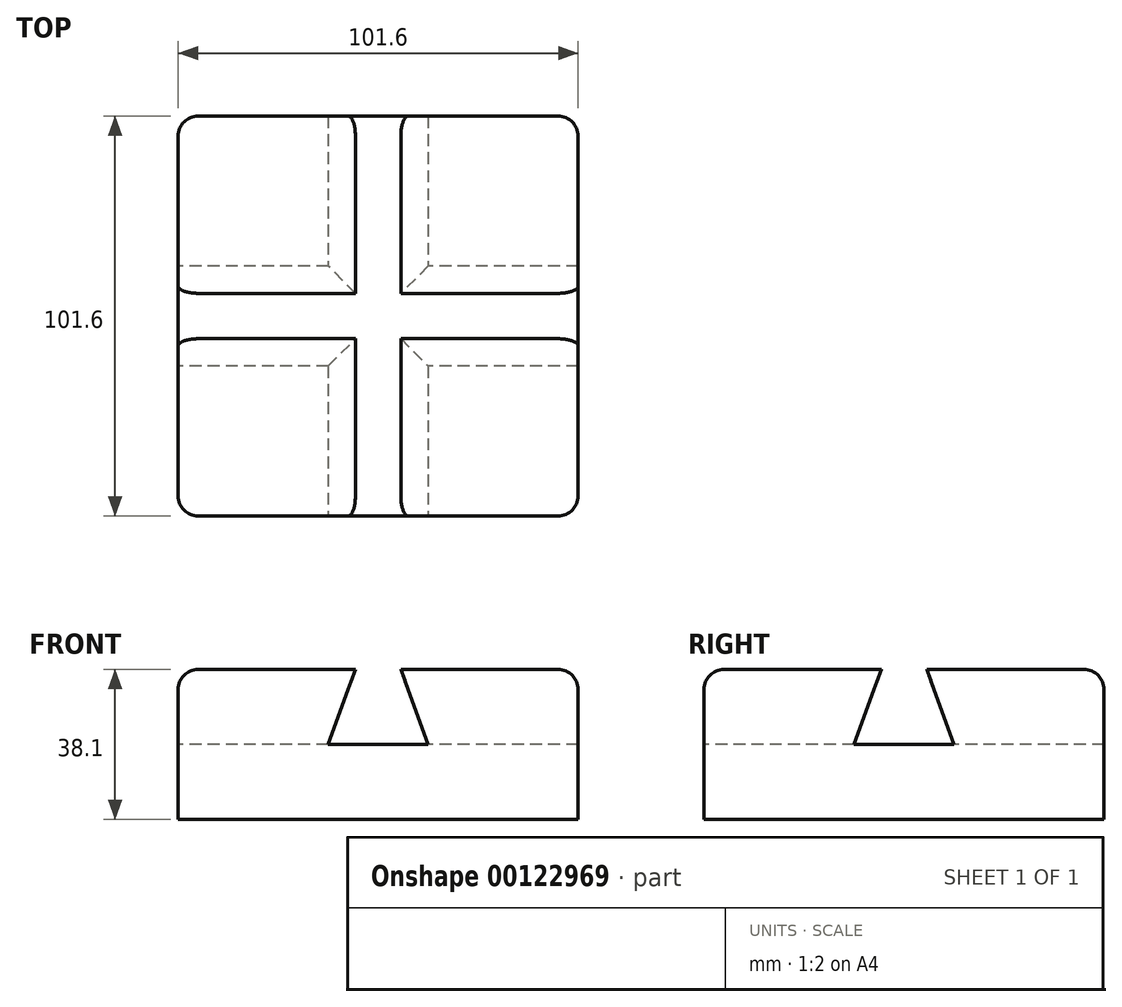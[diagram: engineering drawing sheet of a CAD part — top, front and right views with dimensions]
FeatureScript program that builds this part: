
annotation { "Feature Type Name" : "Feature", "Feature Type Description" : "" }
export const myFeature = defineFeature(function(context is Context, id is Id, definition is map)
    precondition{}
    {
        {
            var Q0;
            Q0=qCreatedBy(makeId("Top.planeOp"),FACE);
            var sketch = newSketch(context, id + "F0", { "sketchPlane" : qUnion([Q0])});
            skLineSegment(sketch, "E0.bottom", {"start": v(-46.22, -52.3) * mm, "end": v(55.38, -52.3) * mm});
            skLineSegment(sketch, "E0.top", {"start": v(-46.22, 49.3) * mm, "end": v(55.38, 49.3) * mm});
            skLineSegment(sketch, "E0.left", {"start": v(-46.22, -52.3) * mm, "end": v(-46.22, 49.3) * mm});
            skLineSegment(sketch, "E0.right", {"start": v(55.38, -52.3) * mm, "end": v(55.38, 49.3) * mm});
            skSolve(sketch);
        }
        {
            var Q0;
            Q0 = qSketchRegion(id + "F0", true);
            extrude(context, id + "F1", {"entities" : qUnion([Q0]), "depth" : 38.1 * mm});
        }
        {
            var Q0;
            Q0=makeQuery(id+"F1.opExtrude","SWEPT_FACE",FACE,{"disambiguationData":[OSD([sQuery(id+"F0.wireOp",EDGE,"E0.bottom")])]});
            var sketch = newSketch(context, id + "F2", { "sketchPlane" : qUnion([Q0])});
            skLineSegment(sketch, "E1", {"start": v(-1.19, 38.1) * mm, "end": v(-8.12, 19.05) * mm});
            skLineSegment(sketch, "E2", {"start": v(-8.12, 19.05) * mm, "end": v(17.28, 19.05) * mm});
            skLineSegment(sketch, "E3", {"start": v(17.28, 19.05) * mm, "end": v(10.34, 38.1) * mm});
            skSolve(sketch);
        }
        {
            var Q0;
            {var subQ0=sQuery(id+"F2.wireOp",EDGE,"E1");Q0=makeQuery(id+"F2.imprint","IMPRINT",FACE,{"disambiguationData":[TD([[makeQuery(id+"F2.imprint","IMPRINT",EDGE,{"derivedFrom":subQ0}),1.0]])]});}
            extrude(context, id + "F3", {"entities" : qUnion([Q0]), "operationType" : NewBodyOperationType.REMOVE, "endBound" : BoundingType.THROUGH_ALL, "oppositeDirection" : true, "depth" : 25.4 * mm});
        }
        {
            var Q0;
            Q0=makeQuery(id+"F1.opExtrude","SWEPT_FACE",FACE,{"disambiguationData":[OSD([sQuery(id+"F0.wireOp",EDGE,"E0.left")])]});
            var sketch = newSketch(context, id + "F4", { "sketchPlane" : qUnion([Q0])});
            skLineSegment(sketch, "E4", {"start": v(-4.26, 38.1) * mm, "end": v(-11.2, 19.05) * mm});
            skLineSegment(sketch, "E5", {"start": v(-11.2, 19.05) * mm, "end": v(14.2, 19.05) * mm});
            skLineSegment(sketch, "E6", {"start": v(14.2, 19.05) * mm, "end": v(7.27, 38.1) * mm});
            skSolve(sketch);
        }
        {
            var Q0;
            {var subQ0=sQuery(id+"F4.wireOp",EDGE,"E4");Q0=makeQuery(id+"F4.imprint","IMPRINT",FACE,{"disambiguationData":[TD([[makeQuery(id+"F4.imprint","IMPRINT",EDGE,{"derivedFrom":subQ0}),1.0]])]});}
            extrude(context, id + "F5", {"entities" : qUnion([Q0]), "operationType" : NewBodyOperationType.REMOVE, "endBound" : BoundingType.THROUGH_ALL, "oppositeDirection" : true, "depth" : 25.4 * mm});
        }
        {
            var Q0;
            {var subQ0=sQuery(id+"F0.wireOp",EDGE,"E0.bottom");var subQ1=sQuery(id+"F0.wireOp",EDGE,"E0.left");Q0=makeQuery(id+"F3.boolean.opBoolean","SPLIT",EDGE,{"disambiguationData":[TD([makeQuery(id+"F1.opExtrude","SWEPT_FACE",FACE,{"disambiguationData":[OSD([subQ1])]})])],"derivedFrom":makeQuery(id+"F1.opExtrude","CAP_EDGE",EDGE,{"disambiguationData":[OSD([subQ0])],"isStart":false})});}
            var Q1;
            {var subQ0=sQuery(id+"F0.wireOp",EDGE,"E0.bottom");var subQ1=sQuery(id+"F0.wireOp",EDGE,"E0.left");Q1=makeQuery(id+"F5.boolean.opBoolean","SPLIT",EDGE,{"disambiguationData":[TD([makeQuery(id+"F1.opExtrude","SWEPT_FACE",FACE,{"disambiguationData":[OSD([subQ0])]})])],"derivedFrom":makeQuery(id+"F1.opExtrude","CAP_EDGE",EDGE,{"disambiguationData":[OSD([subQ1])],"isStart":false})});}
            var Q2;
            {var subQ0=sQuery(id+"F0.wireOp",EDGE,"E0.bottom");var subQ1=sQuery(id+"F0.wireOp",EDGE,"E0.right");Q2=makeQuery(id+"F3.boolean.opBoolean","SPLIT",EDGE,{"disambiguationData":[TD([makeQuery(id+"F1.opExtrude","SWEPT_FACE",FACE,{"disambiguationData":[OSD([subQ1])]})])],"derivedFrom":makeQuery(id+"F1.opExtrude","CAP_EDGE",EDGE,{"disambiguationData":[OSD([subQ0])],"isStart":false})});}
            var Q3;
            {var subQ0=sQuery(id+"F0.wireOp",EDGE,"E0.bottom");var subQ1=sQuery(id+"F0.wireOp",EDGE,"E0.right");Q3=makeQuery(id+"F5.boolean.opBoolean","SPLIT",EDGE,{"disambiguationData":[TD([makeQuery(id+"F1.opExtrude","SWEPT_FACE",FACE,{"disambiguationData":[OSD([subQ0])]})])],"derivedFrom":makeQuery(id+"F1.opExtrude","CAP_EDGE",EDGE,{"disambiguationData":[OSD([subQ1])],"isStart":false})});}
            var Q4;
            {var subQ0=sQuery(id+"F0.wireOp",EDGE,"E0.right");var subQ1=sQuery(id+"F0.wireOp",EDGE,"E0.top");Q4=makeQuery(id+"F5.boolean.opBoolean","SPLIT",EDGE,{"disambiguationData":[TD([makeQuery(id+"F1.opExtrude","SWEPT_FACE",FACE,{"disambiguationData":[OSD([subQ1])]})])],"derivedFrom":makeQuery(id+"F1.opExtrude","CAP_EDGE",EDGE,{"disambiguationData":[OSD([subQ0])],"isStart":false})});}
            var Q5;
            {var subQ0=sQuery(id+"F0.wireOp",EDGE,"E0.right");var subQ1=sQuery(id+"F0.wireOp",EDGE,"E0.top");Q5=makeQuery(id+"F3.boolean.opBoolean","SPLIT",EDGE,{"disambiguationData":[TD([makeQuery(id+"F1.opExtrude","SWEPT_FACE",FACE,{"disambiguationData":[OSD([subQ0])]})])],"derivedFrom":makeQuery(id+"F1.opExtrude","CAP_EDGE",EDGE,{"disambiguationData":[OSD([subQ1])],"isStart":false})});}
            var Q6;
            {var subQ0=sQuery(id+"F0.wireOp",EDGE,"E0.left");var subQ1=sQuery(id+"F0.wireOp",EDGE,"E0.top");Q6=makeQuery(id+"F3.boolean.opBoolean","SPLIT",EDGE,{"disambiguationData":[TD([makeQuery(id+"F1.opExtrude","SWEPT_FACE",FACE,{"disambiguationData":[OSD([subQ0])]})])],"derivedFrom":makeQuery(id+"F1.opExtrude","CAP_EDGE",EDGE,{"disambiguationData":[OSD([subQ1])],"isStart":false})});}
            var Q7;
            {var subQ0=sQuery(id+"F0.wireOp",EDGE,"E0.left");var subQ1=sQuery(id+"F0.wireOp",EDGE,"E0.top");Q7=makeQuery(id+"F5.boolean.opBoolean","SPLIT",EDGE,{"disambiguationData":[TD([makeQuery(id+"F1.opExtrude","SWEPT_FACE",FACE,{"disambiguationData":[OSD([subQ1])]})])],"derivedFrom":makeQuery(id+"F1.opExtrude","CAP_EDGE",EDGE,{"disambiguationData":[OSD([subQ0])],"isStart":false})});}
            var Q8;
            Q8=makeQuery(id+"F1.opExtrude","SWEPT_EDGE",EDGE,{"disambiguationData":[OSD([sQuery(id+"F0.wireOp",EDGE,"E0.bottom"),sQuery(id+"F0.wireOp",EDGE,"E0.left")])]});
            var Q9;
            Q9=makeQuery(id+"F1.opExtrude","SWEPT_EDGE",EDGE,{"disambiguationData":[OSD([sQuery(id+"F0.wireOp",EDGE,"E0.bottom"),sQuery(id+"F0.wireOp",EDGE,"E0.right")])]});
            var Q10;
            Q10=makeQuery(id+"F1.opExtrude","SWEPT_EDGE",EDGE,{"disambiguationData":[OSD([sQuery(id+"F0.wireOp",EDGE,"E0.top"),sQuery(id+"F0.wireOp",EDGE,"E0.left")])]});
            var Q11;
            Q11=makeQuery(id+"F1.opExtrude","SWEPT_EDGE",EDGE,{"disambiguationData":[OSD([sQuery(id+"F0.wireOp",EDGE,"E0.top"),sQuery(id+"F0.wireOp",EDGE,"E0.right")])]});
            fillet(context, id + "F6", {"entities" : qUnion([Q0, Q1, Q2, Q3, Q4, Q5, Q6, Q7, Q8, Q9, Q10, Q11]), "radius" : 5.08 * mm, "tangentPropagation" : true, "allowEdgeOverflow" : false});
        }
    });
